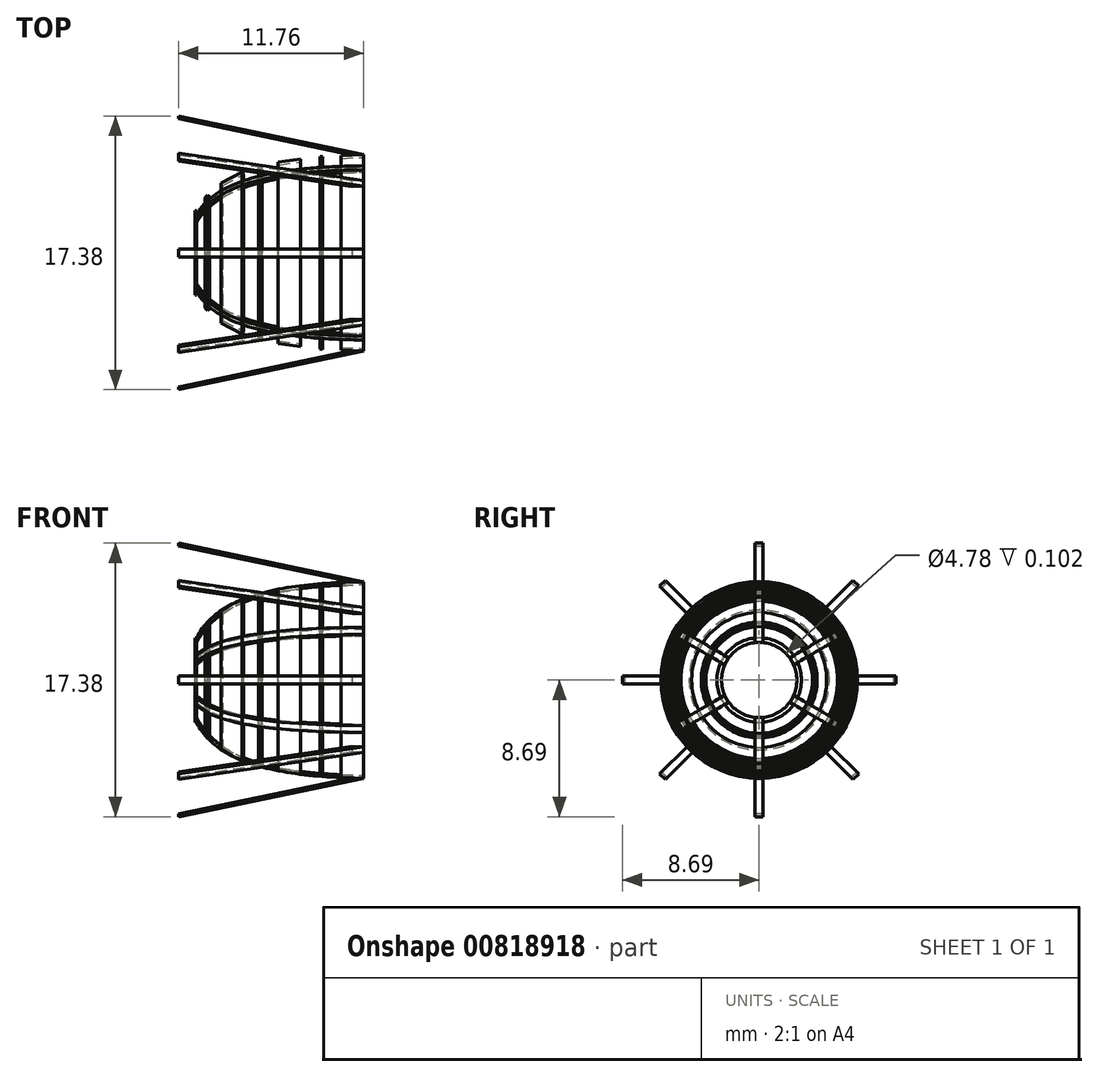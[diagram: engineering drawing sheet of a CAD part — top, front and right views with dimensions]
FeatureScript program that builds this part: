
annotation { "Feature Type Name" : "Feature", "Feature Type Description" : "" }
export const myFeature = defineFeature(function(context is Context, id is Id, definition is map)
    precondition{}
    {
        {
            var Q0;
            Q0=qCreatedBy(makeId("Front.planeOp"),FACE);
            var sketch = newSketch(context, id + "F0", { "sketchPlane" : qUnion([Q0])});
            skFitSpline(sketch, "E0", {"points": [v(0, 2.69) * mm, v(10.6, 6.24) * mm], "startDerivative": vector(4.14, 8.52) * mm, "endDerivative": vector(13.82, 0.2) * mm});
            skFitSpline(sketch, "E1", {"points": [v(0, 2.38) * mm, v(10.6, 6.06) * mm], "startDerivative": vector(4.46, 8.98) * mm, "endDerivative": vector(13.82, 0.2) * mm});
            skLineSegment(sketch, "E2", {"start": v(0, 2.69) * mm, "end": v(0, 2.38) * mm});
            skLineSegment(sketch, "E3", {"start": v(10.6, 6.24) * mm, "end": v(10.6, 6.06) * mm});
            skLineSegment(sketch, "E4", {"start": v(0, -2.69) * mm, "end": v(0, -2.38) * mm});
            skLineSegment(sketch, "E5.MirrorCS", {"start": v(10.6, -6.24) * mm, "end": v(10.6, -6.06) * mm});
            skFitSpline(sketch, "E6.MirrorCS", {"points": [v(0, -2.38) * mm, v(10.6, -6.06) * mm], "startDerivative": vector(4.46, -8.98) * mm, "endDerivative": vector(13.82, -0.2) * mm});
            skFitSpline(sketch, "E7.MirrorCS", {"points": [v(0, -2.69) * mm, v(10.6, -6.24) * mm], "startDerivative": vector(4.14, -8.52) * mm, "endDerivative": vector(13.82, -0.2) * mm});
            skLineSegment(sketch, "E8", {"start": v(0, 0) * mm, "end": v(12.51, 0) * mm, "construction": true});
            skSolve(sketch);
        }
        {
            var Q0;
            Q0=makeQuery(id+"F0.imprint","IMPRINT",FACE,{"disambiguationData":[TD([[makeQuery(id+"F0.imprint","IMPRINT",EDGE,{"derivedFrom":sQuery(id+"F0.wireOp",EDGE,"E0")}),-1.0]])]});
            var Q1;
            Q1=makeQuery(id+"F0.imprint","IMPRINT",FACE,{"disambiguationData":[TD([[makeQuery(id+"F0.imprint","IMPRINT",EDGE,{"derivedFrom":sQuery(id+"F0.wireOp",EDGE,"E4")}),-1.0]])]});
            extrude(context, id + "F1", {"entities" : qUnion([Q0, Q1]), "endBound" : BoundingType.SYMMETRIC, "depth" : 0.5 * mm, "offsetDistance" : 25.4 * mm});
        }
        {
            var Q0;
            Q0=qCreatedBy(makeId("Front.planeOp"),FACE);
            var sketch = newSketch(context, id + "F2", { "sketchPlane" : qUnion([Q0])});
            skLineSegment(sketch, "E9.bottom", {"start": v(0, 2.4) * mm, "end": v(-0.1, 2.4) * mm});
            skLineSegment(sketch, "E9.top", {"start": v(0, 2.68) * mm, "end": v(-0.1, 2.68) * mm});
            skLineSegment(sketch, "E9.left", {"start": v(0, 2.4) * mm, "end": v(0, 2.68) * mm});
            skLineSegment(sketch, "E9.right", {"start": v(-0.1, 2.4) * mm, "end": v(-0.1, 2.68) * mm});
            skLineSegment(sketch, "E10", {"start": v(0.05, 0) * mm, "end": v(4.12, 0) * mm, "construction": true});
            skSolve(sketch);
        }
        {
            var Q0;
            Q0=makeQuery(id+"F2.imprint","IMPRINT",FACE,{"disambiguationData":[TD([[makeQuery(id+"F2.imprint","IMPRINT",EDGE,{"derivedFrom":sQuery(id+"F2.wireOp",EDGE,"E9.bottom")}),-1.0]])]});
            var Q1;
            Q1=sQuery(id+"F2.wireOp",EDGE,"E10");
            revolve(context, id + "F3", {"surfaceOperationType" : NewSurfaceOperationType.NEW, "entities" : qUnion([Q0]), "axis" : qUnion([Q1]), "revolveType" : RevolveType.FULL});
        }
        {
            var Q0;
            Q0=makeQuery(id+"F1.opExtrude","SWEPT_BODY",BODY,{"disambiguationData":[OSD([sQuery(id+"F0.wireOp",EDGE,"E0"),sQuery(id+"F0.wireOp",EDGE,"E1"),sQuery(id+"F0.wireOp",EDGE,"E2"),sQuery(id+"F0.wireOp",EDGE,"E3")])]});
            var Q1;
            Q1=makeQuery(id+"F1.opExtrude","SWEPT_BODY",BODY,{"disambiguationData":[OSD([sQuery(id+"F0.wireOp",EDGE,"E4"),sQuery(id+"F0.wireOp",EDGE,"E5.MirrorCS"),sQuery(id+"F0.wireOp",EDGE,"E6.MirrorCS"),sQuery(id+"F0.wireOp",EDGE,"E7.MirrorCS")])]});
            var Q2;
            Q2=makeQuery(id+"F3.opRevolve","SWEPT_EDGE",EDGE,{"disambiguationData":[OSD([sQuery(id+"F2.wireOp",EDGE,"E9.top"),sQuery(id+"F2.wireOp",EDGE,"E9.left")])]});
            circularPattern(context, id + "F4", {"entities" : qUnion([Q0, Q1]), "axis" : qUnion([Q2]), "angle" : 360 * degree, "instanceCount" : 6, "equalSpace" : true});
        }
        {
            var Q0;
            Q0=qCreatedBy(makeId("Front.planeOp"),FACE);
            var sketch = newSketch(context, id + "F5", { "sketchPlane" : qUnion([Q0])});
            skLineSegment(sketch, "E11.bottom", {"start": v(10.59, 6.25) * mm, "end": v(9.16, 6.18) * mm});
            skLineSegment(sketch, "E11.top", {"start": v(10.6, 6.07) * mm, "end": v(9.17, 6) * mm});
            skLineSegment(sketch, "E11.left", {"start": v(10.59, 6.25) * mm, "end": v(10.6, 6.07) * mm});
            skLineSegment(sketch, "E11.right", {"start": v(9.16, 6.18) * mm, "end": v(9.17, 6) * mm});
            skLineSegment(sketch, "E12.bottom", {"start": v(8, 6.12) * mm, "end": v(7.84, 6.12) * mm});
            skLineSegment(sketch, "E12.top", {"start": v(8, 5.94) * mm, "end": v(7.84, 5.94) * mm});
            skLineSegment(sketch, "E12.left", {"start": v(8, 6.12) * mm, "end": v(8, 5.94) * mm});
            skLineSegment(sketch, "E12.right", {"start": v(7.84, 6.12) * mm, "end": v(7.84, 5.94) * mm});
            skLineSegment(sketch, "E13.bottom", {"start": v(6.59, 5.96) * mm, "end": v(5.17, 5.77) * mm});
            skLineSegment(sketch, "E13.top", {"start": v(6.61, 5.78) * mm, "end": v(5.2, 5.59) * mm});
            skLineSegment(sketch, "E13.left", {"start": v(6.59, 5.96) * mm, "end": v(6.61, 5.78) * mm});
            skLineSegment(sketch, "E13.right", {"start": v(5.17, 5.77) * mm, "end": v(5.2, 5.59) * mm});
            skLineSegment(sketch, "E14.bottom", {"start": v(4.12, 5.5) * mm, "end": v(3.94, 5.46) * mm});
            skLineSegment(sketch, "E14.top", {"start": v(4.17, 5.34) * mm, "end": v(3.99, 5.29) * mm});
            skLineSegment(sketch, "E14.left", {"start": v(4.12, 5.5) * mm, "end": v(4.17, 5.34) * mm});
            skLineSegment(sketch, "E14.right", {"start": v(3.94, 5.46) * mm, "end": v(3.99, 5.29) * mm});
            skLineSegment(sketch, "E15.bottom", {"start": v(2.9, 5.14) * mm, "end": v(1.56, 4.45) * mm});
            skLineSegment(sketch, "E15.top", {"start": v(2.98, 4.98) * mm, "end": v(1.64, 4.29) * mm});
            skLineSegment(sketch, "E15.left", {"start": v(2.9, 5.14) * mm, "end": v(2.98, 4.98) * mm});
            skLineSegment(sketch, "E15.right", {"start": v(1.56, 4.45) * mm, "end": v(1.64, 4.29) * mm});
            skLineSegment(sketch, "E16.bottom", {"start": v(0.69, 3.68) * mm, "end": v(0.54, 3.5) * mm});
            skLineSegment(sketch, "E16.top", {"start": v(0.83, 3.56) * mm, "end": v(0.68, 3.39) * mm});
            skLineSegment(sketch, "E16.left", {"start": v(0.69, 3.68) * mm, "end": v(0.83, 3.56) * mm});
            skLineSegment(sketch, "E16.right", {"start": v(0.54, 3.5) * mm, "end": v(0.68, 3.39) * mm});
            skLineSegment(sketch, "E17", {"start": v(0, 0) * mm, "end": v(11.03, 0) * mm, "construction": true});
            skSolve(sketch);
        }
        {
            var Q0;
            Q0=qSketchRegion(id+"F5",true);
            var Q1;
            Q1=sQuery(id+"F5.wireOp",EDGE,"E17");
            revolve(context, id + "F6", {"surfaceOperationType" : NewSurfaceOperationType.NEW, "entities" : qUnion([Q0]), "axis" : qUnion([Q1]), "revolveType" : RevolveType.FULL});
        }
        {
            var Q0;
            Q0=qCreatedBy(makeId("Front.planeOp"),FACE);
            var sketch = newSketch(context, id + "F7", { "sketchPlane" : qUnion([Q0])});
            skLineSegment(sketch, "E18", {"start": v(0, 0) * mm, "end": v(-1.16, 0) * mm, "construction": true});
            skLineSegment(sketch, "E19", {"start": v(-1.16, 0) * mm, "end": v(-1.16, 8.7) * mm, "construction": true});
            skLineSegment(sketch, "E20", {"start": v(-1.16, 8.7) * mm, "end": v(10.6, 6.24) * mm});
            skLineSegment(sketch, "E21", {"start": v(10.6, 6.24) * mm, "end": v(9.88, 6.21) * mm});
            skLineSegment(sketch, "E22", {"start": v(9.88, 6.21) * mm, "end": v(-1.16, 8.52) * mm});
            skLineSegment(sketch, "E23", {"start": v(-1.16, 8.52) * mm, "end": v(-1.16, 8.7) * mm});
            skSolve(sketch);
        }
        {
            var Q0;
            Q0=makeQuery(id+"F7.imprint","IMPRINT",FACE,{"disambiguationData":[TD([[makeQuery(id+"F7.imprint","IMPRINT",EDGE,{"derivedFrom":sQuery(id+"F7.wireOp",EDGE,"E20")}),-1.0]])]});
            extrude(context, id + "F8", {"entities" : qUnion([Q0]), "endBound" : BoundingType.SYMMETRIC, "depth" : 0.5 * mm, "offsetDistance" : 25.4 * mm});
        }
        {
            var Q0;
            Q0=makeQuery(id+"F8.opExtrude","SWEPT_BODY",BODY,{"disambiguationData":[OSD([sQuery(id+"F7.wireOp",EDGE,"E20"),sQuery(id+"F7.wireOp",EDGE,"E21"),sQuery(id+"F7.wireOp",EDGE,"E22"),sQuery(id+"F7.wireOp",EDGE,"E23")])]});
            var Q1;
            Q1=makeQuery(id+"F6.opRevolve","SWEPT_EDGE",EDGE,{"disambiguationData":[OSD([sQuery(id+"F5.wireOp",EDGE,"E11.bottom"),sQuery(id+"F5.wireOp",EDGE,"E11.right")])]});
            circularPattern(context, id + "F9", {"entities" : qUnion([Q0]), "axis" : qUnion([Q1]), "angle" : 360 * degree, "instanceCount" : 8, "equalSpace" : true});
        }
    });
